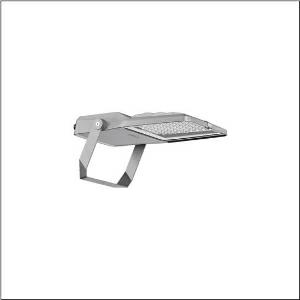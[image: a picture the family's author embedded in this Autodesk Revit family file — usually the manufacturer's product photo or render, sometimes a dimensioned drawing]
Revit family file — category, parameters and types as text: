
# Revit family: floodlight_fl_21_iq_mini___pl33t_5xa7772b5f1a_9cd7
name_source: partatom
category: Lighting Fixtures
units: mm (PartAtom-declared; Revit-internal decimal feet)

## family parameters
Cut with Voids When Loaded = No
Host = Face
Light Source = No
Part Type = Normal
Room Calculation Point = No
Round Connector Dimension = Use Diameter
Shared = No

## types (1)
- --- (1 x LED, 5750 lm, 45.5 W, 4000K)
    Apparent Load = 46 VA
    CIE Flux Codes = 26 75 99 100 100
    Color Rendering = 80
    Color Temperature = 4000K
    Default Elevation = 1800 mm
    Description = Floodlight FL 21 iQ mini, floodlight, primary light control with lens, of PMMA, primary optical cover: protective disc, of toughened safety glass, transparent, light distribution: PL33T, light emission: direct distribution, installation type: surface-mounted, lamps: LED, High Power LED, rated values: 5.750lm | 45,5W | 126,4lm/W (begin service life); end service life: 5.750lm | 48W; at 50% lumin. flux: 2.875lm | 21,5W | 133,7lm/W, colour temperature: 4000K, colour rendering: CRI > 80, light colour: 840, light setting 1 begin service life: 100% | 5.750lm | 45,5W | 126,4lm/W | 4.000K, light setting 1 end service life: 48W, further light settings possible, control: Street-Remote, Auto-Match, Temp-Guard, Night-Set, Smart-Wire, Desk-Remote (wireless, voltage-free reading and setting of iQ features in the workshop via application-optimized NFC function/RFID function), optimised constant luminous flux control (CLO 2.0), pre-setting: linear dimming characteristic, with terminal, 6-pole, mains connection: 220..240V, AC, 50/60Hz, luminaire housing, of diecast aluminium, powder-coated, SITECO metallic grey (DB 702S), corrosivity category C5 mid according to DIN EN ISO 12944suitable for swimming poolschlorine-resistant, sealing non-destructively replaceable, mounting bracket, of steel, galvanised, powder-coated, SITECO metallic grey (DB 702S), protection rating (complete): IP66, insulation class (complete): insulation class II (safety insulation), certification: CE, ENEC, VDE, protection symbol: D, impact resistance: IK08, permissible operating ambient temperature: -40..+40°C, permissible operating ambient temperature for outdoor applications: -40..+50°C, standard: DIN EN 12944, LABS conformity tested according to VDMA 24364:2018-05, packaging unit: 1 piece

Light Distribution: PL33T
    Height = 70 mm
    Lamp = 1 x LED
    Lamp Light Flux = 5750 lm
    Lamp Power = 45.5 W
    Lamp count = 1
    Length = 485 mm
    Luminous efficacy = 126 lm/W
    Manufacturer = Siteco
    ModVariant = No
    Model = 5XA7772B5F1A
    Number of Poles = 1
    OnlyDefault = Yes
    Power Factor = 1
    Product Name = Floodlight FL 21 iQ mini | PL33T
    Product group = floodlight | pylon annexe
    ProductGroupID = 6201
    Protection Class = Protection class II
    Protection Degree = IP 66
    RLX_Detail_Level = 1
    RLX_Emergency_Light_Flux = 0 lm
    RLX_Emergency_Type = 0
    RLX_Emergency_Type_DB = No
    RlxData = <blob elided: 96265 chars, md5=1f247ecd>
    Socket = socket
    Standby Power = 0 W
    System Light Flux = 5750 lm
    System Power = 46 W
    Type Comments = factory setting: luminous flux: 100 % | dim-lin: 254 | 463 mA
    Type Image = l_1006845.jpg
    URL = http://relux.com
    VarID = @adj_149347
    Voltage = 0 V
    Weight = 0.00 kg
    Width = 337 mm

## geometry (parser evidence)
native form markers: Blend x4, Sweep x13
no freeform markers — native parametric forms only
